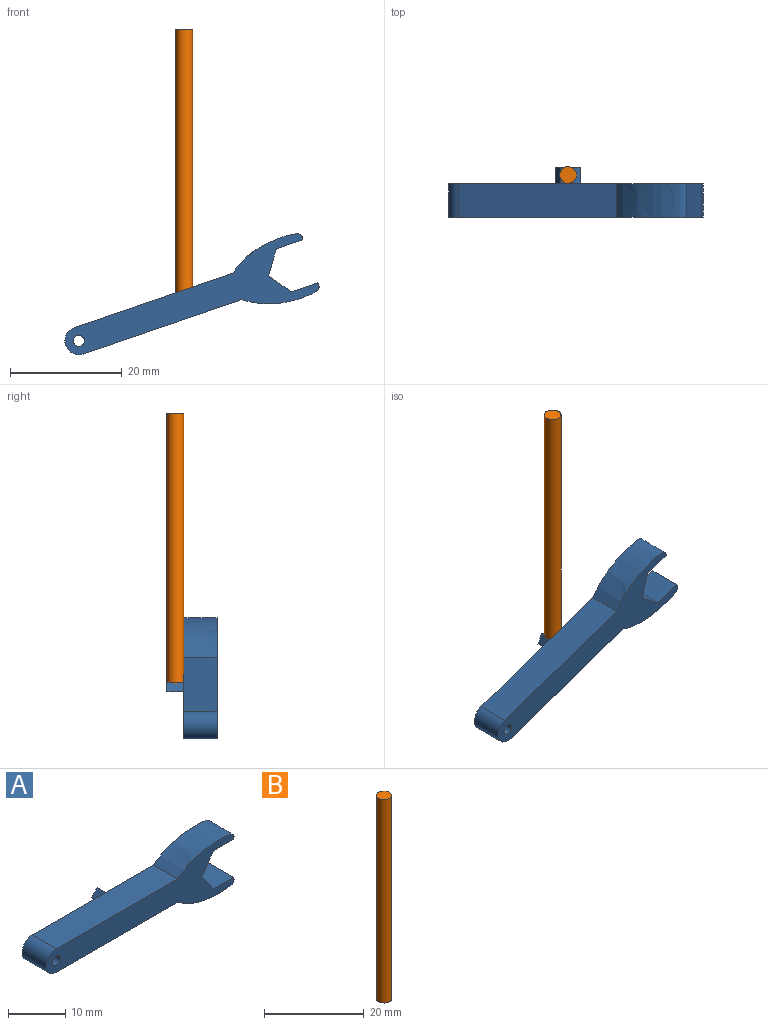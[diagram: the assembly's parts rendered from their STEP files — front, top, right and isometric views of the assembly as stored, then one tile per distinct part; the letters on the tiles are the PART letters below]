
ASSEMBLY  parts=2 mates=1
PART A: 16 faces, bbox 46.6x9x11.8 mm
  f0: extruded ~13.94x6mm, area 93.8mm2, adj f1,f8,f10,f11
  f1: plane 30x6mm, normal (0,0,1), area 180mm2, adj f0,f2,f10,f11
  f2: cylinder r=2.5mm len=6mm, axis (0,1,0), area 47.1mm2, adj f1,f3,f10,f11
  f3: plane 30x6mm, normal (0,0,-1), area 180mm2, adj f2,f4,f10,f11
  f4: extruded ~13.94x6mm, area 93.8mm2, adj f3,f5,f10,f11
  f5: plane 6x5mm, normal (0,0,1), area 30mm2, adj f4,f6,f10,f11
  f6: plane 6x4.1mm, normal (0.82,0,0.57), area 30mm2, adj f5,f7,f10,f11
  f7: plane 6x4.1mm, normal (0.82,0,-0.57), area 30mm2, adj f6,f8,f10,f11
  f8: plane 6x5mm, normal (0,0,-1), area 30mm2, adj f0,f7,f10,f11
  f9: cylinder r=1mm len=6mm, axis (0,1,0), area 37.7mm2, adj f10,f11
  f10: plane 46.6x11.77mm, normal (0,-1,0), area 241.5mm2, adj f0,f1,f2,f3,f4,f5,f6,f7
  f11: plane 46.6x11.77mm, normal (0,1,0), area 237.5mm2, adj f0,f1,f2,f3,f4,f5,f6,f7
  f12: plane 3x2.85mm, normal (0.71,0,0.7), area 12mm2, adj f11,f13,f14,f15
  f13: plane 4.23x3mm, normal (-0.33,0,-0.95), area 13.4mm2, adj f11,f12,f14,f15
  f14: plane 3x1.43mm, normal (-0.7,0,0.71), area 6mm2, adj f11,f12,f13,f15
  f15: plane 4.23x2.85mm, normal (0,1,0), area 4mm2, adj f12,f13,f14
PART B: 3 faces, bbox 3x3x50 mm
  f0: cylinder r=1.5mm len=50mm, axis (0,0,-1), area 471.2mm2, adj f1,f2
  f1: plane 3x3mm, normal (0,0,1), area 7.1mm2, adj f0
  f2: plane 3x3mm, normal (0,0,-1), area 7.1mm2, adj f0
PLACE A rot(axis=(0,-1,0),19deg) t=(-18.89,-1.5,-5.89)mm
PLACE B at identity
MATE fastened A.f13 <-> B.f0  axis (0,0,-1) through (0,0,0)mm
